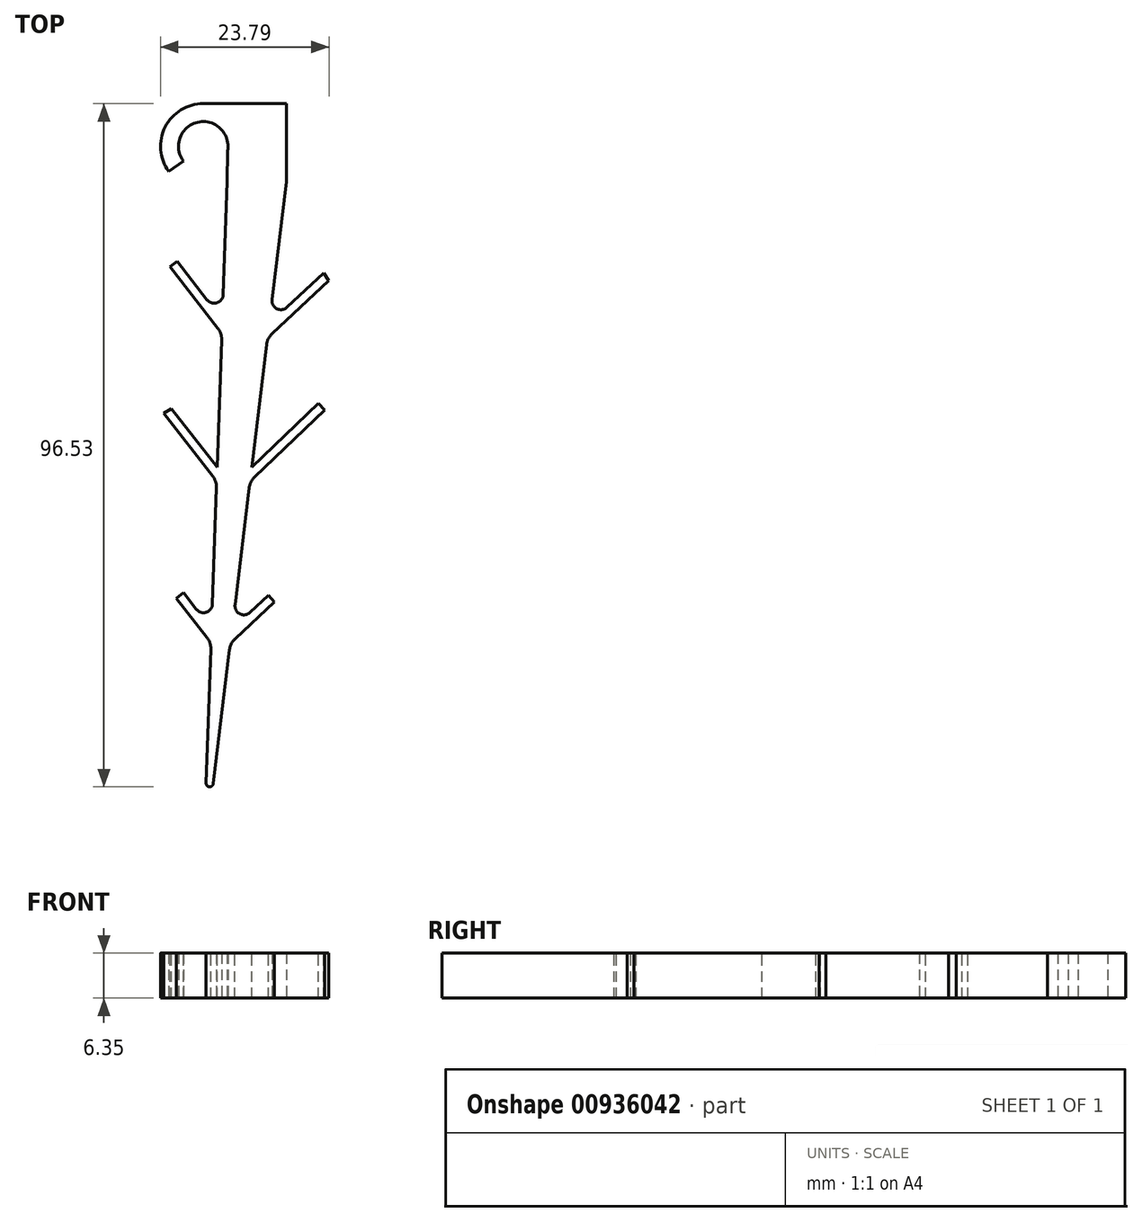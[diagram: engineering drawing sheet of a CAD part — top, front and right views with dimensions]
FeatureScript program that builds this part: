
annotation { "Feature Type Name" : "Feature", "Feature Type Description" : "" }
export const myFeature = defineFeature(function(context is Context, id is Id, definition is map)
    precondition{}
    {
        {
            var Q0;
            Q0=qCreatedBy(makeId("Top.planeOp"),FACE);
            var sketch = newSketch(context, id + "F0", { "sketchPlane" : qUnion([Q0])});
            skArc(sketch, "E0", {"start": v(3.43, 41.03) * mm, "mid": v(-0.8, 45.07) * mm, "end": v(-2.8, 39.58) * mm});
            skArc(sketch, "E1.0", {"start": v(0, 47.7) * mm, "mid": v(-5.37, 44.41) * mm, "end": v(-4.88, 38.13) * mm});
            skLineSegment(sketch, "E2", {"start": v(-2.8, 39.58) * mm, "end": v(-4.88, 38.13) * mm});
            skLineSegment(sketch, "E3", {"start": v(11.75, 36.67) * mm, "end": v(11.75, 47.7) * mm});
            skLineSegment(sketch, "E4", {"start": v(11.75, 47.7) * mm, "end": v(0, 47.7) * mm});
            skLineSegment(sketch, "E5", {"start": v(3.38, 36.67) * mm, "end": v(0, -60.1) * mm});
            skLineSegment(sketch, "E6", {"start": v(11.75, 36.67) * mm, "end": v(0, -60.1) * mm});
            skLineSegment(sketch, "E7", {"start": v(3.43, 41.03) * mm, "end": v(3.38, 36.67) * mm});
            skSolve(sketch);
        }
        {
            var Q0;
            Q0=makeQuery(id+"F0.imprint","IMPRINT",FACE,{"disambiguationData":[TD([[makeQuery(id+"F0.imprint","IMPRINT",EDGE,{"derivedFrom":sQuery(id+"F0.wireOp",EDGE,"E0")}),-1.0]])]});
            extrude(context, id + "F1", {"entities" : qUnion([Q0]), "depth" : 6.35 * mm, "offsetDistance" : 25.4 * mm});
        }
        {
            var Q0;
            Q0=makeQuery(id+"F1.opExtrude","CAP_FACE",FACE,{"disambiguationData":[OSD([sQuery(id+"F0.wireOp",EDGE,"E0"),sQuery(id+"F0.wireOp",EDGE,"E1.0"),sQuery(id+"F0.wireOp",EDGE,"E2"),sQuery(id+"F0.wireOp",EDGE,"E3"),sQuery(id+"F0.wireOp",EDGE,"E4"),sQuery(id+"F0.wireOp",EDGE,"E5"),sQuery(id+"F0.wireOp",EDGE,"E6"),sQuery(id+"F0.wireOp",EDGE,"E7")])],"isStart":false});
            var sketch = newSketch(context, id + "F2", { "sketchPlane" : qUnion([Q0])});
            skLineSegment(sketch, "E8", {"start": v(-3.7, 25.42) * mm, "end": v(5.8, 13.27) * mm});
            skLineSegment(sketch, "E9", {"start": v(5.8, 13.27) * mm, "end": v(17.05, 23.8) * mm});
            skLineSegment(sketch, "E10", {"start": v(-4.5, 4.6) * mm, "end": v(1.97, -3.67) * mm});
            skLineSegment(sketch, "E11", {"start": v(6.85, -3.67) * mm, "end": v(16.28, 5.36) * mm});
            skLineSegment(sketch, "E12", {"start": v(1.17, -26.48) * mm, "end": v(-2.8, -21.4) * mm});
            skLineSegment(sketch, "E13", {"start": v(4.07, -26.56) * mm, "end": v(9.2, -21.76) * mm});
            skLineSegment(sketch, "E14.0", {"start": v(5.66, 11.4) * mm, "end": v(17.76, 22.71) * mm});
            skLineSegment(sketch, "E15.0", {"start": v(-4.7, 24.64) * mm, "end": v(5.66, 11.4) * mm});
            skLineSegment(sketch, "E16", {"start": v(17.05, 23.8) * mm, "end": v(17.76, 22.71) * mm});
            skLineSegment(sketch, "E17", {"start": v(16.28, 5.36) * mm, "end": v(17.15, 4.43) * mm});
            skLineSegment(sketch, "E18", {"start": v(17.15, 4.43) * mm, "end": v(6.6, -5.66) * mm});
            skLineSegment(sketch, "E19", {"start": v(6.6, -5.66) * mm, "end": v(6.85, -3.67) * mm});
            skLineSegment(sketch, "E20", {"start": v(1.97, -3.67) * mm, "end": v(1.9, -5.64) * mm});
            skLineSegment(sketch, "E21", {"start": v(1.9, -5.64) * mm, "end": v(-5.6, 3.96) * mm});
            skLineSegment(sketch, "E22", {"start": v(-5.6, 3.96) * mm, "end": v(-4.5, 4.6) * mm});
            skLineSegment(sketch, "E23", {"start": v(3.83, -28.52) * mm, "end": v(10.08, -22.68) * mm});
            skLineSegment(sketch, "E24", {"start": v(10.08, -22.68) * mm, "end": v(9.2, -21.76) * mm});
            skLineSegment(sketch, "E25", {"start": v(4.07, -26.56) * mm, "end": v(3.83, -28.52) * mm});
            skLineSegment(sketch, "E26", {"start": v(-2.8, -21.4) * mm, "end": v(-3.8, -22.18) * mm});
            skLineSegment(sketch, "E27", {"start": v(-3.8, -22.18) * mm, "end": v(1.1, -28.45) * mm});
            skLineSegment(sketch, "E28", {"start": v(1.1, -28.45) * mm, "end": v(1.17, -26.48) * mm});
            skLineSegment(sketch, "E29", {"start": v(-3.7, 25.42) * mm, "end": v(-4.7, 24.64) * mm});
            skSolve(sketch);
        }
        {
            var Q0;
            Q0 = qSketchRegion(id + "F2", true);
            var Q1;
            Q1=makeQuery(id+"F1.opExtrude","CAP_FACE",FACE,{"disambiguationData":[OSD([sQuery(id+"F0.wireOp",EDGE,"E0"),sQuery(id+"F0.wireOp",EDGE,"E1.0"),sQuery(id+"F0.wireOp",EDGE,"E2"),sQuery(id+"F0.wireOp",EDGE,"E3"),sQuery(id+"F0.wireOp",EDGE,"E4"),sQuery(id+"F0.wireOp",EDGE,"E5"),sQuery(id+"F0.wireOp",EDGE,"E6"),sQuery(id+"F0.wireOp",EDGE,"E7")])],"isStart":true});
            extrude(context, id + "F3", {"entities" : qUnion([Q0]), "operationType" : NewBodyOperationType.ADD, "endBound" : BoundingType.UP_TO_SURFACE, "oppositeDirection" : true, "depth" : 25.4 * mm, "endBoundEntityFace" : qUnion([Q1]), "offsetDistance" : 25.4 * mm});
        }
        {
            var Q0;
            Q0=makeQuery(id+"F3.boolean.opBoolean","INTERSECT",EDGE,{"derivedFrom":[makeQuery(id+"F1.opExtrude","SWEPT_FACE",FACE,{"disambiguationData":[OSD([sQuery(id+"F0.wireOp",EDGE,"E5")])]}),makeQuery(id+"F3.opExtrude","SWEPT_FACE",FACE,{"disambiguationData":[OSD([sQuery(id+"F2.wireOp",EDGE,"E15.0")])]})]});
            var Q1;
            Q1=makeQuery(id+"F3.boolean.opBoolean","INTERSECT",EDGE,{"derivedFrom":[makeQuery(id+"F1.opExtrude","SWEPT_FACE",FACE,{"disambiguationData":[OSD([sQuery(id+"F0.wireOp",EDGE,"E6")])]}),makeQuery(id+"F3.opExtrude","SWEPT_FACE",FACE,{"disambiguationData":[OSD([sQuery(id+"F2.wireOp",EDGE,"E14.0")])]})]});
            var Q2;
            Q2=makeQuery(id+"F3.opExtrude","SWEPT_EDGE",EDGE,{"disambiguationData":[OSD([sQuery(id+"F0.wireOp",EDGE,"E6"),sQuery(id+"F2.wireOp",EDGE,"E18"),sQuery(id+"F2.wireOp",EDGE,"E19")])]});
            var Q3;
            Q3=makeQuery(id+"F3.opExtrude","SWEPT_EDGE",EDGE,{"disambiguationData":[OSD([sQuery(id+"F0.wireOp",EDGE,"E5"),sQuery(id+"F2.wireOp",EDGE,"E20"),sQuery(id+"F2.wireOp",EDGE,"E21")])]});
            var Q4;
            Q4=makeQuery(id+"F3.opExtrude","SWEPT_EDGE",EDGE,{"disambiguationData":[OSD([sQuery(id+"F0.wireOp",EDGE,"E5"),sQuery(id+"F2.wireOp",EDGE,"E27"),sQuery(id+"F2.wireOp",EDGE,"E28")])]});
            var Q5;
            Q5=makeQuery(id+"F3.opExtrude","SWEPT_EDGE",EDGE,{"disambiguationData":[OSD([sQuery(id+"F0.wireOp",EDGE,"E6"),sQuery(id+"F2.wireOp",EDGE,"E23"),sQuery(id+"F2.wireOp",EDGE,"E25")])]});
            fillet(context, id + "F4", {"entities" : qUnion([Q0, Q1, Q2, Q3, Q4, Q5]), "radius" : 2.54 * mm, "tangentPropagation" : true, "allowEdgeOverflow" : false});
        }
        {
            var Q0;
            Q0=makeQuery(id+"F3.boolean.opBoolean","INTERSECT",EDGE,{"derivedFrom":[makeQuery(id+"F1.opExtrude","SWEPT_FACE",FACE,{"disambiguationData":[OSD([sQuery(id+"F0.wireOp",EDGE,"E5")])]}),makeQuery(id+"F3.opExtrude","SWEPT_FACE",FACE,{"disambiguationData":[OSD([sQuery(id+"F2.wireOp",EDGE,"E8")])]})]});
            var Q1;
            Q1=makeQuery(id+"F3.boolean.opBoolean","INTERSECT",EDGE,{"derivedFrom":[makeQuery(id+"F1.opExtrude","SWEPT_FACE",FACE,{"disambiguationData":[OSD([sQuery(id+"F0.wireOp",EDGE,"E6")])]}),makeQuery(id+"F3.opExtrude","SWEPT_FACE",FACE,{"disambiguationData":[OSD([sQuery(id+"F2.wireOp",EDGE,"E9")])]})]});
            var Q2;
            Q2=makeQuery(id+"F3.opExtrude","SWEPT_EDGE",EDGE,{"disambiguationData":[OSD([sQuery(id+"F0.wireOp",EDGE,"E6"),sQuery(id+"F2.wireOp",EDGE,"E11"),sQuery(id+"F2.wireOp",EDGE,"E19")])]});
            var Q3;
            Q3=makeQuery(id+"F3.opExtrude","SWEPT_EDGE",EDGE,{"disambiguationData":[OSD([sQuery(id+"F0.wireOp",EDGE,"E5"),sQuery(id+"F2.wireOp",EDGE,"E10"),sQuery(id+"F2.wireOp",EDGE,"E20")])]});
            var Q4;
            Q4=makeQuery(id+"F3.opExtrude","SWEPT_EDGE",EDGE,{"disambiguationData":[OSD([sQuery(id+"F0.wireOp",EDGE,"E5"),sQuery(id+"F2.wireOp",EDGE,"E12"),sQuery(id+"F2.wireOp",EDGE,"E28")])]});
            var Q5;
            Q5=makeQuery(id+"F3.opExtrude","SWEPT_EDGE",EDGE,{"disambiguationData":[OSD([sQuery(id+"F0.wireOp",EDGE,"E6"),sQuery(id+"F2.wireOp",EDGE,"E13"),sQuery(id+"F2.wireOp",EDGE,"E25")])]});
            fillet(context, id + "F5", {"entities" : qUnion([Q0, Q1, Q2, Q3, Q4, Q5]), "radius" : 1.27 * mm, "tangentPropagation" : true, "allowEdgeOverflow" : false});
        }
        {
            var Q0;
            Q0=makeQuery(id+"F1.opExtrude","SWEPT_EDGE",EDGE,{"disambiguationData":[OSD([sQuery(id+"F0.wireOp",EDGE,"E5"),sQuery(id+"F0.wireOp",EDGE,"E6")])]});
            fillet(context, id + "F6", {"entities" : qUnion([Q0]), "radius" : 0.5 * mm, "tangentPropagation" : true, "allowEdgeOverflow" : false});
        }
    });
